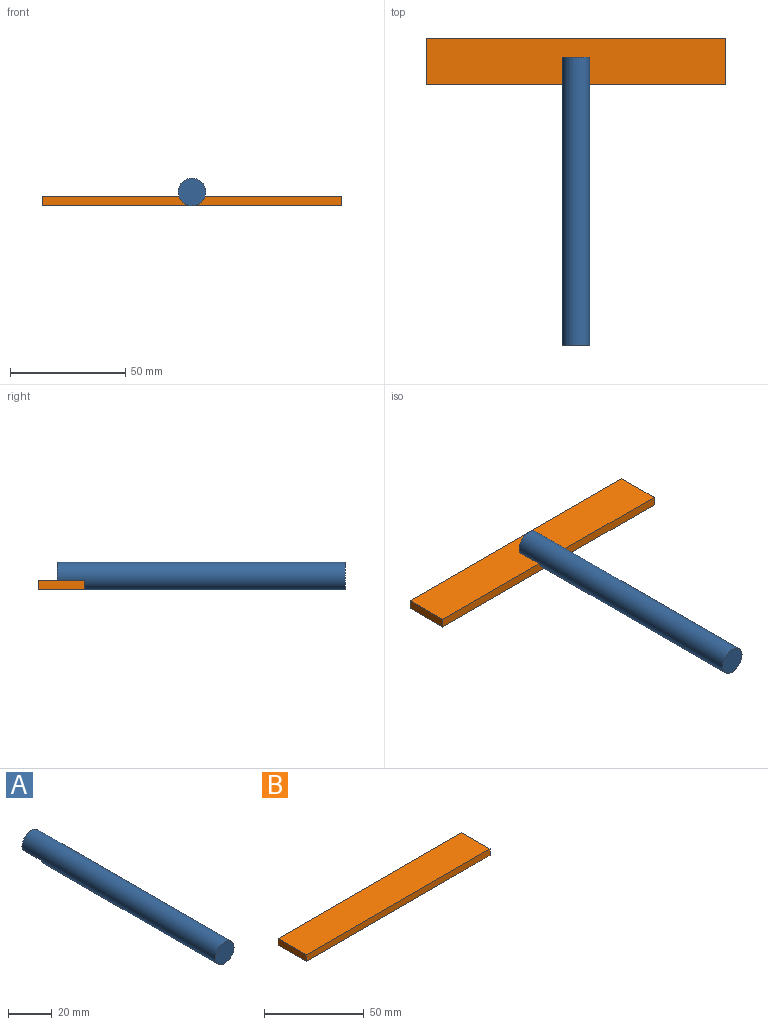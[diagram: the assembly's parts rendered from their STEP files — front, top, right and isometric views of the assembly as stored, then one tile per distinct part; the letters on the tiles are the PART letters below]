
ASSEMBLY  parts=2 mates=1
PART A: 5 faces, bbox 12x125x12 mm
  f0: cylinder r=6mm len=125mm, axis (0,1,0), area 4535.1mm2, adj f1,f2,f3,f4
  f1: plane 12x12mm, normal (0,-1,0), area 113.1mm2, adj f0
  f2: plane 12x8mm, normal (0,1,0), area 80.1mm2, adj f0,f4
  f3: plane 11.31x4mm, normal (0,1,0), area 33mm2, adj f0,f4
  f4: plane 12x11.31mm, normal (0,0,-1), area 135.8mm2, adj f0,f2,f3
PART B: 6 faces, bbox 130x20x4 mm
  f0: plane 20x4mm, normal (1,0,0), area 80mm2, adj f1,f3,f4,f5
  f1: plane 130x4mm, normal (0,1,0), area 520mm2, adj f0,f2,f4,f5
  f2: plane 20x4mm, normal (-1,0,0), area 80mm2, adj f1,f3,f4,f5
  f3: plane 130x4mm, normal (0,-1,0), area 520mm2, adj f0,f2,f4,f5
  f4: plane 130x20mm, normal (0,0,1), area 2600mm2, adj f0,f1,f2,f3
  f5: plane 130x20mm, normal (0,0,-1), area 2600mm2, adj f0,f1,f2,f3
PLACE A at identity
PLACE B t=(0,10,-4)mm
MATE fastened B.f4 <-> A.f4  axis (0,0,1) through (0,10,0)mm
